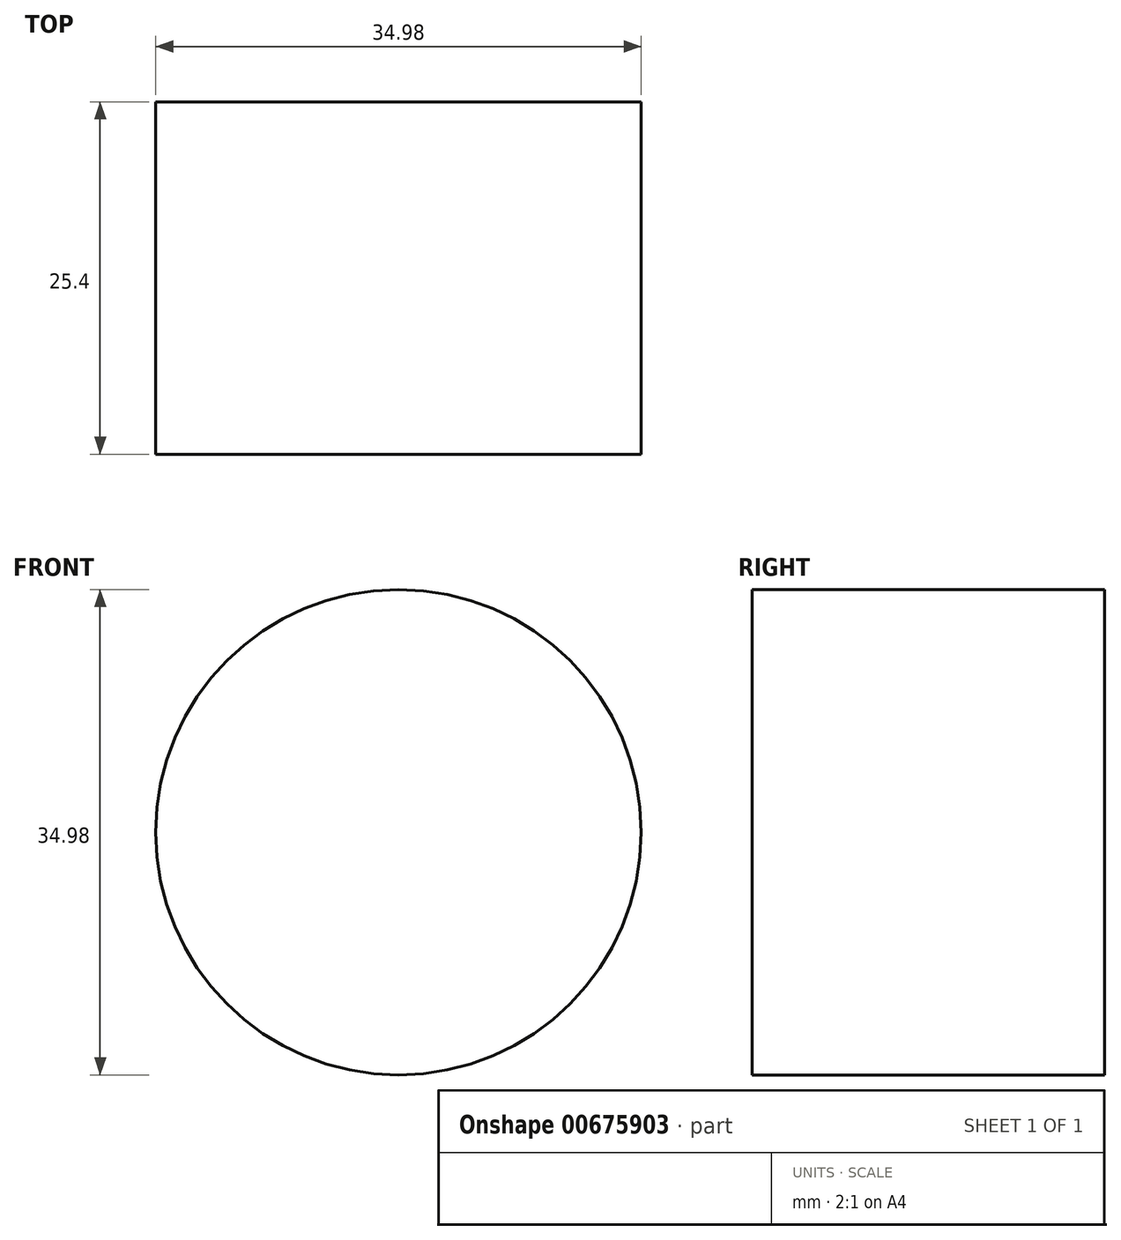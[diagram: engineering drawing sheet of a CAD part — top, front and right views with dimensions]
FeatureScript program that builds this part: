
annotation { "Feature Type Name" : "Feature", "Feature Type Description" : "" }
export const myFeature = defineFeature(function(context is Context, id is Id, definition is map)
    precondition{}
    {
        {
            var Q0;
            Q0=qCreatedBy(makeId("Front.planeOp"),FACE);
            var sketch = newSketch(context, id + "F0", { "sketchPlane" : qUnion([Q0])});
            skCircle(sketch, "E0", {"center": v(0, 0) * mm, "radius": 17.5 * mm});
            skSolve(sketch);
        }
        {
            var Q0;
            Q0=makeQuery(id+"F0.imprint","IMPRINT",FACE,{"disambiguationData":[TD([[makeQuery(id+"F0.imprint","IMPRINT",EDGE,{"derivedFrom":sQuery(id+"F0.wireOp",EDGE,"E0")}),1.0]])]});
            extrude(context, id + "F1", {"entities" : qUnion([Q0]), "depth" : 25.4 * mm, "offsetDistance" : 25.4 * mm});
        }
    });
